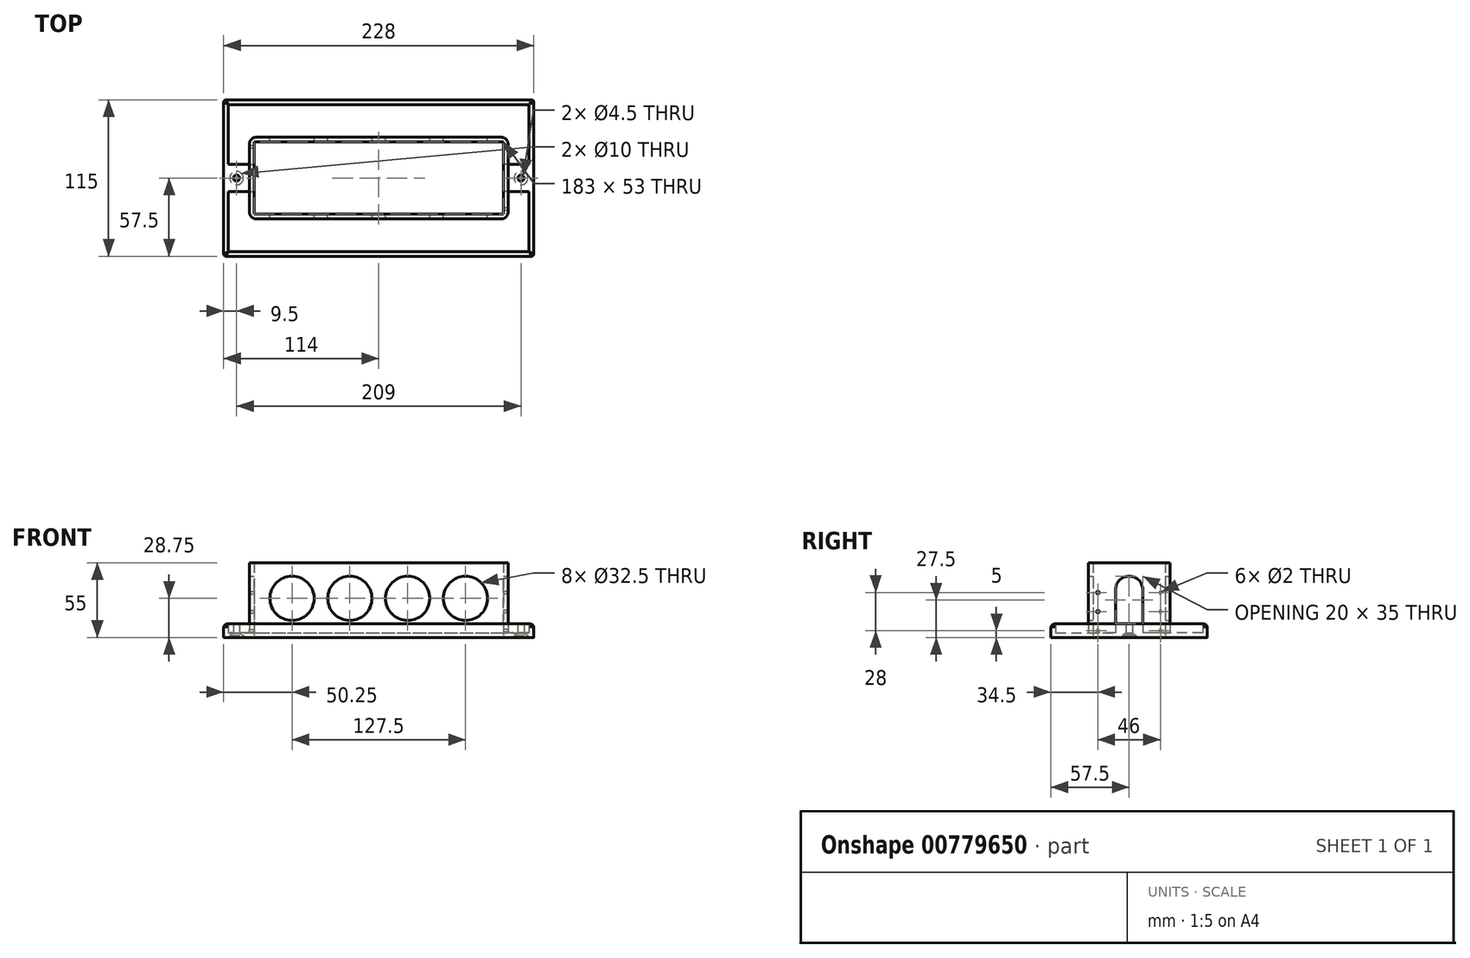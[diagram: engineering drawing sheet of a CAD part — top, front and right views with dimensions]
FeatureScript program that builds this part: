
annotation { "Feature Type Name" : "Feature", "Feature Type Description" : "" }
export const myFeature = defineFeature(function(context is Context, id is Id, definition is map)
    precondition{}
    {
        {
            var Q0;
            Q0=qCreatedBy(makeId("Top.planeOp"),FACE);
            var sketch = newSketch(context, id + "F0", { "sketchPlane" : qUnion([Q0])});
            skLineSegment(sketch, "E0.bottom", {"start": v(114, -57.5) * mm, "end": v(-114, -57.5) * mm});
            skLineSegment(sketch, "E0.top", {"start": v(114, 57.5) * mm, "end": v(-114, 57.5) * mm});
            skLineSegment(sketch, "E0.left", {"start": v(114, -57.5) * mm, "end": v(114, 57.5) * mm});
            skLineSegment(sketch, "E0.right", {"start": v(-114, -57.5) * mm, "end": v(-114, 57.5) * mm});
            skPoint(sketch, "E0.middle", {"position": v(0, 0) * mm});
            skLineSegment(sketch, "E1.bottom", {"start": v(-91.5, 26.5) * mm, "end": v(91.5, 26.5) * mm});
            skLineSegment(sketch, "E1.top", {"start": v(-91.5, -26.5) * mm, "end": v(91.5, -26.5) * mm});
            skLineSegment(sketch, "E1.left", {"start": v(-91.5, 26.5) * mm, "end": v(-91.5, -26.5) * mm});
            skLineSegment(sketch, "E1.right", {"start": v(91.5, 26.5) * mm, "end": v(91.5, -26.5) * mm});
            skLineSegment(sketch, "E2.bottom", {"start": v(-95, 30) * mm, "end": v(95, 30) * mm});
            skLineSegment(sketch, "E2.top", {"start": v(-95, -30) * mm, "end": v(95, -30) * mm});
            skLineSegment(sketch, "E2.left", {"start": v(-95, 30) * mm, "end": v(-95, -30) * mm});
            skLineSegment(sketch, "E2.right", {"start": v(95, 30) * mm, "end": v(95, -30) * mm});
            skCircle(sketch, "E3", {"center": v(-104.5, 0) * mm, "radius": 5 * mm});
            skCircle(sketch, "E4", {"center": v(104.5, 0) * mm, "radius": 5 * mm});
            skCircle(sketch, "E5", {"center": v(104.5, 0) * mm, "radius": 2.25 * mm});
            skCircle(sketch, "E6", {"center": v(-104.5, 0) * mm, "radius": 2.25 * mm});
            skLineSegment(sketch, "E7", {"start": v(-110.5, 54) * mm, "end": v(110.5, 54) * mm});
            skLineSegment(sketch, "E8", {"start": v(110.5, 54) * mm, "end": v(110.5, 10) * mm});
            skLineSegment(sketch, "E9", {"start": v(110.5, 10) * mm, "end": v(95, 10) * mm});
            skLineSegment(sketch, "E10", {"start": v(-110.5, 54) * mm, "end": v(-110.5, 10) * mm});
            skLineSegment(sketch, "E11", {"start": v(-110.5, 10) * mm, "end": v(-95, 10) * mm});
            skLineSegment(sketch, "E12", {"start": v(-95, -10) * mm, "end": v(-110.5, -10) * mm});
            skLineSegment(sketch, "E13", {"start": v(-110.5, -10) * mm, "end": v(-110.5, -54) * mm});
            skLineSegment(sketch, "E14", {"start": v(-110.5, -54) * mm, "end": v(110.5, -54) * mm});
            skLineSegment(sketch, "E15", {"start": v(110.5, -54) * mm, "end": v(110.5, -10) * mm});
            skLineSegment(sketch, "E16", {"start": v(110.5, -10) * mm, "end": v(95, -10) * mm});
            skSolve(sketch);
        }
        {
            var Q0;
            Q0=makeQuery(id+"F0.imprint","IMPRINT",FACE,{"disambiguationData":[TD([[makeQuery(id+"F0.imprint","IMPRINT",EDGE,{"derivedFrom":sQuery(id+"F0.wireOp",EDGE,"E1.bottom")}),1.0]])]});
            extrude(context, id + "F1", {"entities" : qUnion([Q0]), "depth" : 55 * mm, "offsetDistance" : 25 * mm});
        }
        {
            var Q0;
            Q0=makeQuery(id+"F0.imprint","IMPRINT",FACE,{"disambiguationData":[TD([[makeQuery(id+"F0.imprint","IMPRINT",EDGE,{"derivedFrom":sQuery(id+"F0.wireOp",EDGE,"E0.bottom")}),-1.0]])]});
            extrude(context, id + "F2", {"entities" : qUnion([Q0]), "operationType" : NewBodyOperationType.ADD, "depth" : 10 * mm, "offsetDistance" : 25 * mm});
        }
        {
            var Q0;
            Q0=makeQuery(id+"F0.imprint","IMPRINT",FACE,{"disambiguationData":[TD([[makeQuery(id+"F0.imprint","IMPRINT",EDGE,{"derivedFrom":sQuery(id+"F0.wireOp",EDGE,"E4")}),1.0]])]});
            var Q1;
            Q1=makeQuery(id+"F0.imprint","IMPRINT",FACE,{"disambiguationData":[TD([[makeQuery(id+"F0.imprint","IMPRINT",EDGE,{"derivedFrom":sQuery(id+"F0.wireOp",EDGE,"E3")}),1.0]])]});
            extrude(context, id + "F3", {"entities" : qUnion([Q0, Q1]), "operationType" : NewBodyOperationType.ADD, "depth" : 10 * mm, "offsetDistance" : 25 * mm});
        }
        {
            var Q0;
            Q0=sQuery(id+"F0.wireOp",VERTEX,"E3.center");
            var Q1;
            Q1=sQuery(id+"F0.wireOp",VERTEX,"E4.center");
            var Q2;
            Q2=makeQuery(id+"F1.opExtrude","SWEPT_BODY",BODY,{"disambiguationData":[OSD([sQuery(id+"F0.wireOp",EDGE,"E1.bottom"),sQuery(id+"F0.wireOp",EDGE,"E1.top"),sQuery(id+"F0.wireOp",EDGE,"E1.left"),sQuery(id+"F0.wireOp",EDGE,"E1.right"),sQuery(id+"F0.wireOp",EDGE,"E2.bottom"),sQuery(id+"F0.wireOp",EDGE,"E2.top"),sQuery(id+"F0.wireOp",EDGE,"E2.left"),sQuery(id+"F0.wireOp",EDGE,"E2.right")])]});
            hole(context, id + "F4", {"style" : HoleStyle.SIMPLE, "endStyle" : HoleEndStyle.BLIND, "oppositeDirection" : true, "holeDiameter" : 10 * mm, "majorDiameter" : 5 * mm, "holeDepth" : 1.5 * mm, "isTappedThrough" : true, "tappedDepth" : 12 * mm, "tapClearance" : 3, "locations" : qUnion([Q0, Q1]), "scope" : qUnion([Q2])});
        }
        {
            var Q0;
            Q0=makeQuery(id+"F2.opExtrude","CAP_EDGE",EDGE,{"disambiguationData":[OSD([sQuery(id+"F0.wireOp",EDGE,"E0.right")])],"isStart":false});
            var Q1;
            Q1=makeQuery(id+"F2.opExtrude","CAP_EDGE",EDGE,{"disambiguationData":[OSD([sQuery(id+"F0.wireOp",EDGE,"E0.top")])],"isStart":false});
            var Q2;
            Q2=makeQuery(id+"F2.opExtrude","CAP_EDGE",EDGE,{"disambiguationData":[OSD([sQuery(id+"F0.wireOp",EDGE,"E0.bottom")])],"isStart":false});
            var Q3;
            Q3=makeQuery(id+"F2.opExtrude","CAP_EDGE",EDGE,{"disambiguationData":[OSD([sQuery(id+"F0.wireOp",EDGE,"E0.left")])],"isStart":false});
            fillet(context, id + "F5", {"entities" : qUnion([Q0, Q1, Q2, Q3]), "radius" : 3 * mm, "tangentPropagation" : true, "allowEdgeOverflow" : false});
        }
        {
            var Q0;
            Q0=makeQuery(id+"F2.opExtrude","SWEPT_EDGE",EDGE,{"disambiguationData":[OSD([sQuery(id+"F0.wireOp",EDGE,"E0.top"),sQuery(id+"F0.wireOp",EDGE,"E0.left")])]});
            var Q1;
            Q1=makeQuery(id+"F2.opExtrude","SWEPT_EDGE",EDGE,{"disambiguationData":[OSD([sQuery(id+"F0.wireOp",EDGE,"E0.bottom"),sQuery(id+"F0.wireOp",EDGE,"E0.left")])]});
            var Q2;
            Q2=makeQuery(id+"F2.opExtrude","SWEPT_EDGE",EDGE,{"disambiguationData":[OSD([sQuery(id+"F0.wireOp",EDGE,"E0.bottom"),sQuery(id+"F0.wireOp",EDGE,"E0.right")])]});
            var Q3;
            Q3=makeQuery(id+"F2.opExtrude","SWEPT_EDGE",EDGE,{"disambiguationData":[OSD([sQuery(id+"F0.wireOp",EDGE,"E0.top"),sQuery(id+"F0.wireOp",EDGE,"E0.right")])]});
            fillet(context, id + "F6", {"entities" : qUnion([Q0, Q1, Q2, Q3]), "radius" : 2 * mm, "tangentPropagation" : true, "allowEdgeOverflow" : false});
        }
        {
            var Q0;
            Q0=makeQuery(id+"F1.opExtrude","SWEPT_FACE",FACE,{"disambiguationData":[OSD([sQuery(id+"F0.wireOp",EDGE,"E1.right")])]});
            var sketch = newSketch(context, id + "F7", { "sketchPlane" : qUnion([Q0])});
            skLineSegment(sketch, "E17.bottom", {"start": v(-10, 10) * mm, "end": v(10, 10) * mm});
            skLineSegment(sketch, "E17.top", {"start": v(-10, 45) * mm, "end": v(10, 45) * mm});
            skLineSegment(sketch, "E17.left", {"start": v(-10, 10) * mm, "end": v(-10, 45) * mm});
            skLineSegment(sketch, "E17.right", {"start": v(10, 10) * mm, "end": v(10, 45) * mm});
            skCircle(sketch, "E18", {"center": v(23, 5) * mm, "radius": 1 * mm});
            skCircle(sketch, "E19", {"center": v(23, 19) * mm, "radius": 1 * mm});
            skCircle(sketch, "E20", {"center": v(23, 33) * mm, "radius": 1 * mm});
            skSolve(sketch);
        }
        {
            var Q0;
            Q0=makeQuery(id+"F1.opExtrude","SWEPT_FACE",FACE,{"disambiguationData":[OSD([sQuery(id+"F0.wireOp",EDGE,"E1.left")])]});
            var sketch = newSketch(context, id + "F8", { "sketchPlane" : qUnion([Q0])});
            skLineSegment(sketch, "E21.bottom", {"start": v(10, 45) * mm, "end": v(-10, 45) * mm});
            skLineSegment(sketch, "E21.top", {"start": v(10, 10) * mm, "end": v(-10, 10) * mm});
            skLineSegment(sketch, "E21.left", {"start": v(10, 45) * mm, "end": v(10, 10) * mm});
            skLineSegment(sketch, "E21.right", {"start": v(-10, 45) * mm, "end": v(-10, 10) * mm});
            skCircle(sketch, "E22", {"center": v(23, 5) * mm, "radius": 1 * mm});
            skCircle(sketch, "E23", {"center": v(23, 19) * mm, "radius": 1 * mm});
            skCircle(sketch, "E24", {"center": v(23, 33) * mm, "radius": 1 * mm});
            skSolve(sketch);
        }
        {
            var Q0;
            Q0=qSketchRegion(id+"F7",true);
            var Q1;
            Q1=makeQuery(id+"F7.imprint","IMPRINT",FACE,{"disambiguationData":[TD([[makeQuery(id+"F7.imprint","IMPRINT",EDGE,{"derivedFrom":sQuery(id+"F7.wireOp",EDGE,"E17.bottom")}),1.0]])]});
            extrude(context, id + "F9", {"entities" : qUnion([Q0, Q1]), "operationType" : NewBodyOperationType.REMOVE, "oppositeDirection" : true, "depth" : 15 * mm, "offsetDistance" : 25 * mm});
        }
        {
            var Q0;
            Q0=qSketchRegion(id+"F8",true);
            var Q1;
            Q1=makeQuery(id+"F8.imprint","IMPRINT",FACE,{"disambiguationData":[TD([[makeQuery(id+"F8.imprint","IMPRINT",EDGE,{"derivedFrom":sQuery(id+"F8.wireOp",EDGE,"E21.bottom")}),1.0]])]});
            extrude(context, id + "F10", {"entities" : qUnion([Q0, Q1]), "operationType" : NewBodyOperationType.REMOVE, "oppositeDirection" : true, "depth" : 15 * mm, "offsetDistance" : 25 * mm});
        }
        {
            var Q0;
            Q0=makeQuery(id+"F10.boolean.opBoolean","COPY",EDGE,{"derivedFrom":makeQuery(id+"F10.opExtrude","SWEPT_EDGE",EDGE,{"disambiguationData":[OSD([sQuery(id+"F8.wireOp",EDGE,"E21.bottom"),sQuery(id+"F8.wireOp",EDGE,"E21.left")])]})});
            var Q1;
            Q1=makeQuery(id+"F10.boolean.opBoolean","COPY",EDGE,{"derivedFrom":makeQuery(id+"F10.opExtrude","SWEPT_EDGE",EDGE,{"disambiguationData":[OSD([sQuery(id+"F8.wireOp",EDGE,"E21.bottom"),sQuery(id+"F8.wireOp",EDGE,"E21.right")])]})});
            fillet(context, id + "F11", {"entities" : qUnion([Q0, Q1]), "radius" : 10 * mm, "tangentPropagation" : true, "allowEdgeOverflow" : false});
        }
        {
            var Q0;
            Q0=makeQuery(id+"F9.boolean.opBoolean","COPY",EDGE,{"derivedFrom":makeQuery(id+"F9.opExtrude","SWEPT_EDGE",EDGE,{"disambiguationData":[OSD([sQuery(id+"F7.wireOp",EDGE,"E17.top"),sQuery(id+"F7.wireOp",EDGE,"E17.left")])]})});
            var Q1;
            Q1=makeQuery(id+"F9.boolean.opBoolean","COPY",EDGE,{"derivedFrom":makeQuery(id+"F9.opExtrude","SWEPT_EDGE",EDGE,{"disambiguationData":[OSD([sQuery(id+"F7.wireOp",EDGE,"E17.top"),sQuery(id+"F7.wireOp",EDGE,"E17.right")])]})});
            fillet(context, id + "F12", {"entities" : qUnion([Q0, Q1]), "radius" : 10 * mm, "tangentPropagation" : true, "allowEdgeOverflow" : false});
        }
        {
            var Q0;
            Q0=makeQuery(id+"F7.imprint","IMPRINT",FACE,{"disambiguationData":[TD([[makeQuery(id+"F7.imprint","IMPRINT",EDGE,{"derivedFrom":sQuery(id+"F7.wireOp",EDGE,"E18")}),1.0]])]});
            extrude(context, id + "F13", {"entities" : qUnion([Q0]), "operationType" : NewBodyOperationType.REMOVE, "oppositeDirection" : true, "depth" : 18 * mm, "offsetDistance" : 25 * mm});
        }
        {
            var Q0;
            Q0=makeQuery(id+"F1.opExtrude","SWEPT_EDGE",EDGE,{"disambiguationData":[OSD([sQuery(id+"F0.wireOp",EDGE,"E2.top"),sQuery(id+"F0.wireOp",EDGE,"E2.left")])]});
            var Q1;
            Q1=makeQuery(id+"F1.opExtrude","SWEPT_EDGE",EDGE,{"disambiguationData":[OSD([sQuery(id+"F0.wireOp",EDGE,"E2.bottom"),sQuery(id+"F0.wireOp",EDGE,"E2.left")])]});
            var Q2;
            Q2=makeQuery(id+"F1.opExtrude","SWEPT_EDGE",EDGE,{"disambiguationData":[OSD([sQuery(id+"F0.wireOp",EDGE,"E2.bottom"),sQuery(id+"F0.wireOp",EDGE,"E2.right")])]});
            var Q3;
            Q3=makeQuery(id+"F1.opExtrude","SWEPT_EDGE",EDGE,{"disambiguationData":[OSD([sQuery(id+"F0.wireOp",EDGE,"E2.top"),sQuery(id+"F0.wireOp",EDGE,"E2.right")])]});
            fillet(context, id + "F14", {"entities" : qUnion([Q0, Q1, Q2, Q3]), "radius" : 5 * mm, "tangentPropagation" : true, "allowEdgeOverflow" : false});
        }
        {
            var Q0;
            {var subQ2=sQuery(id+"F0.wireOp",EDGE,"E2.top");Q0=makeQuery(id+"F0.imprint","IMPRINT",FACE,{"disambiguationData":[TD([[makeQuery(id+"F0.imprint","IMPRINT",EDGE,{"derivedFrom":subQ2}),-1.0]])]});}
            var Q1;
            {var subQ1=sQuery(id+"F0.wireOp",EDGE,"E2.bottom");Q1=makeQuery(id+"F0.imprint","IMPRINT",FACE,{"disambiguationData":[TD([[makeQuery(id+"F0.imprint","IMPRINT",EDGE,{"derivedFrom":subQ1}),1.0]])]});}
            extrude(context, id + "F15", {"entities" : qUnion([Q0, Q1]), "operationType" : NewBodyOperationType.ADD, "depth" : 3.5 * mm, "offsetDistance" : 25 * mm});
        }
        {
            var Q0;
            Q0=makeQuery(id+"F15.opExtrude","SWEPT_EDGE",EDGE,{"disambiguationData":[OSD([sQuery(id+"F0.wireOp",EDGE,"E2.bottom"),sQuery(id+"F0.wireOp",EDGE,"E2.left")])]});
            var Q1;
            Q1=makeQuery(id+"F15.opExtrude","SWEPT_EDGE",EDGE,{"disambiguationData":[OSD([sQuery(id+"F0.wireOp",EDGE,"E2.top"),sQuery(id+"F0.wireOp",EDGE,"E2.left")])]});
            var Q2;
            Q2=makeQuery(id+"F15.opExtrude","SWEPT_EDGE",EDGE,{"disambiguationData":[OSD([sQuery(id+"F0.wireOp",EDGE,"E2.bottom"),sQuery(id+"F0.wireOp",EDGE,"E2.right")])]});
            var Q3;
            Q3=makeQuery(id+"F15.opExtrude","SWEPT_EDGE",EDGE,{"disambiguationData":[OSD([sQuery(id+"F0.wireOp",EDGE,"E2.top"),sQuery(id+"F0.wireOp",EDGE,"E2.right")])]});
            fillet(context, id + "F16", {"entities" : qUnion([Q0, Q1, Q2, Q3]), "radius" : 5 * mm, "tangentPropagation" : true, "allowEdgeOverflow" : false});
        }
        {
            var Q0;
            Q0=makeQuery(id+"F1.opExtrude","SWEPT_FACE",FACE,{"disambiguationData":[OSD([sQuery(id+"F0.wireOp",EDGE,"E2.bottom")])]});
            var sketch = newSketch(context, id + "F17", { "sketchPlane" : qUnion([Q0])});
            skCircle(sketch, "E25", {"center": v(-63.75, 28.75) * mm, "radius": 16.25 * mm});
            skCircle(sketch, "E26", {"center": v(-21.25, 28.75) * mm, "radius": 16.25 * mm});
            skCircle(sketch, "E27", {"center": v(21.25, 28.75) * mm, "radius": 16.25 * mm});
            skCircle(sketch, "E28", {"center": v(63.75, 28.75) * mm, "radius": 16.25 * mm});
            skSolve(sketch);
        }
        {
            var Q0;
            Q0=makeQuery(id+"F17.imprint","IMPRINT",FACE,{"disambiguationData":[TD([[makeQuery(id+"F17.imprint","IMPRINT",EDGE,{"derivedFrom":sQuery(id+"F17.wireOp",EDGE,"E25")}),1.0]])]});
            var Q1;
            Q1=makeQuery(id+"F17.imprint","IMPRINT",FACE,{"disambiguationData":[TD([[makeQuery(id+"F17.imprint","IMPRINT",EDGE,{"derivedFrom":sQuery(id+"F17.wireOp",EDGE,"E26")}),1.0]])]});
            var Q2;
            Q2=makeQuery(id+"F17.imprint","IMPRINT",FACE,{"disambiguationData":[TD([[makeQuery(id+"F17.imprint","IMPRINT",EDGE,{"derivedFrom":sQuery(id+"F17.wireOp",EDGE,"E27")}),1.0]])]});
            var Q3;
            Q3=makeQuery(id+"F17.imprint","IMPRINT",FACE,{"disambiguationData":[TD([[makeQuery(id+"F17.imprint","IMPRINT",EDGE,{"derivedFrom":sQuery(id+"F17.wireOp",EDGE,"E28")}),1.0]])]});
            extrude(context, id + "F18", {"entities" : qUnion([Q0, Q1, Q2, Q3]), "operationType" : NewBodyOperationType.REMOVE, "oppositeDirection" : true, "depth" : 80 * mm, "offsetDistance" : 25 * mm});
        }
    });
